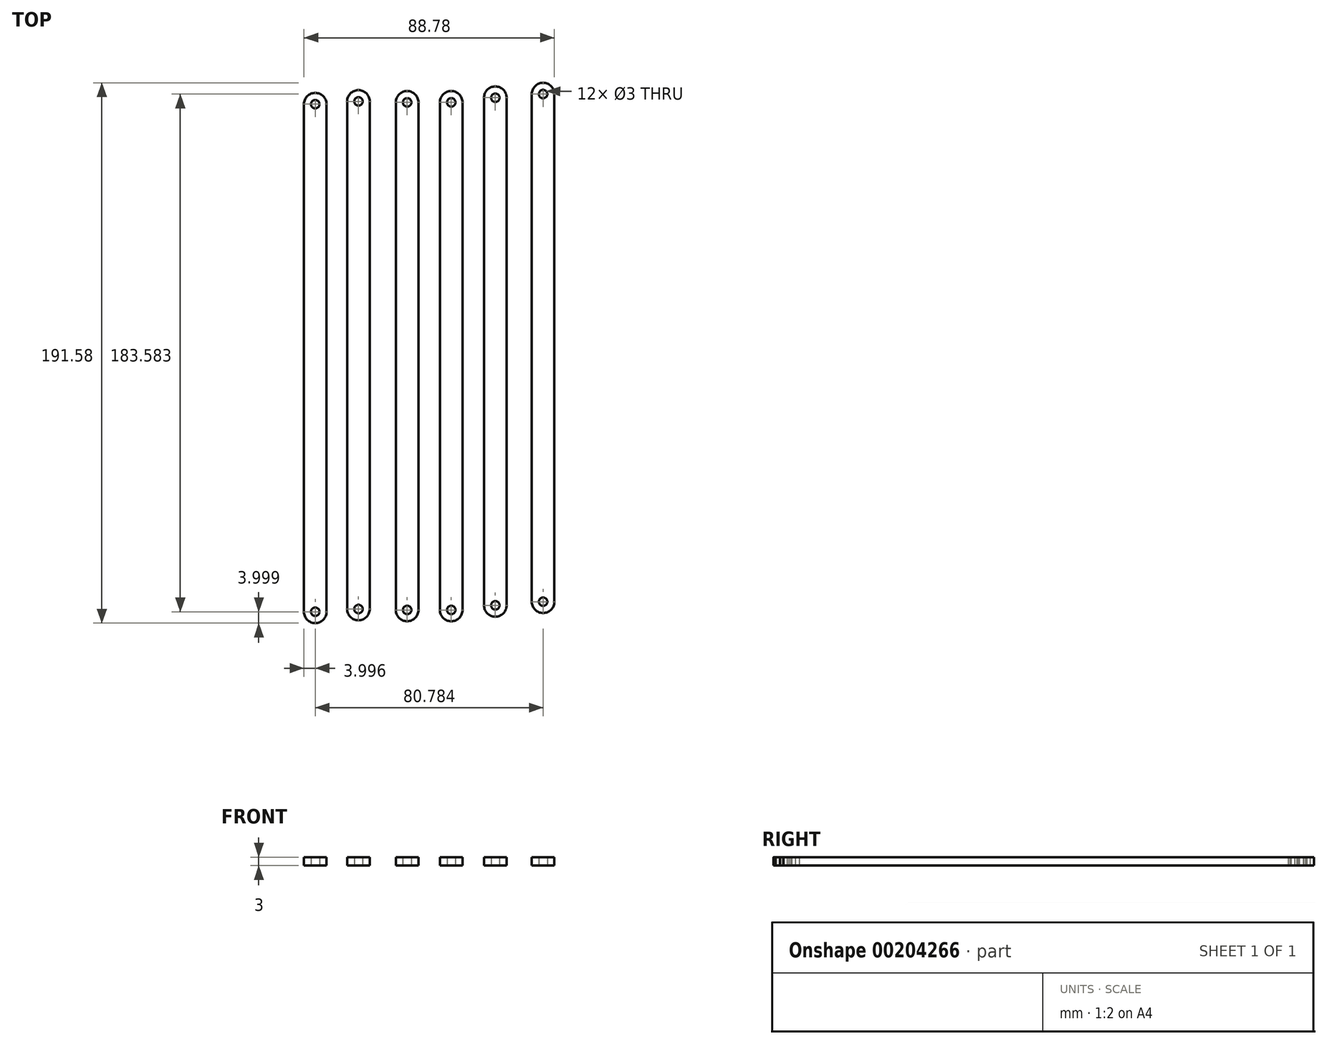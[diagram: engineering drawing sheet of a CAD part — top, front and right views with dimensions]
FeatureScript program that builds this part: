
annotation { "Feature Type Name" : "Feature", "Feature Type Description" : "" }
export const myFeature = defineFeature(function(context is Context, id is Id, definition is map)
    precondition{}
    {
        {
            var Q0;
            Q0=qCreatedBy(makeId("Top.planeOp"),FACE);
            var sketch = newSketch(context, id + "F0", { "sketchPlane" : qUnion([Q0])});
            skLineSegment(sketch, "E0", {"start": v(0, 90) * mm, "end": v(0, -90) * mm, "construction": true});
            skArc(sketch, "E1", {"start": v(4, 90) * mm, "mid": v(0, 94) * mm, "end": v(-4, 90) * mm});
            skArc(sketch, "E2", {"start": v(-4, -90) * mm, "mid": v(0, -94) * mm, "end": v(4, -90) * mm});
            skLineSegment(sketch, "E3", {"start": v(-4, 90) * mm, "end": v(-4, -90) * mm});
            skLineSegment(sketch, "E4.MirrorCS", {"start": v(4, 90) * mm, "end": v(4, -90) * mm});
            skCircle(sketch, "E5", {"center": v(0, 90) * mm, "radius": 1.5 * mm});
            skCircle(sketch, "E6", {"center": v(0, -90) * mm, "radius": 1.5 * mm});
            skLineSegment(sketch, "E7", {"start": v(-17.26, 90.33) * mm, "end": v(-17.26, -89.67) * mm, "construction": true});
            skArc(sketch, "E8", {"start": v(-13.26, 90.33) * mm, "mid": v(-17.26, 94.33) * mm, "end": v(-21.26, 90.33) * mm});
            skArc(sketch, "E9", {"start": v(-21.26, -89.67) * mm, "mid": v(-17.26, -93.67) * mm, "end": v(-13.26, -89.67) * mm});
            skLineSegment(sketch, "E10", {"start": v(-21.26, 90.33) * mm, "end": v(-21.26, -89.67) * mm});
            skLineSegment(sketch, "E11.MirrorCS", {"start": v(-13.26, 90.33) * mm, "end": v(-13.26, -89.67) * mm});
            skCircle(sketch, "E12", {"center": v(-17.26, 90.33) * mm, "radius": 1.5 * mm});
            skCircle(sketch, "E13", {"center": v(-17.26, -89.67) * mm, "radius": 1.5 * mm});
            skLineSegment(sketch, "E14", {"start": v(15.64, 90) * mm, "end": v(15.64, -90) * mm, "construction": true});
            skArc(sketch, "E15", {"start": v(19.64, 90) * mm, "mid": v(15.64, 94) * mm, "end": v(11.64, 90) * mm});
            skArc(sketch, "E16", {"start": v(11.64, -90) * mm, "mid": v(15.64, -94) * mm, "end": v(19.64, -90) * mm});
            skLineSegment(sketch, "E17", {"start": v(11.64, 90) * mm, "end": v(11.64, -90) * mm});
            skLineSegment(sketch, "E18.MirrorCS", {"start": v(19.64, 90) * mm, "end": v(19.64, -90) * mm});
            skCircle(sketch, "E19", {"center": v(15.64, 90) * mm, "radius": 1.5 * mm});
            skCircle(sketch, "E20", {"center": v(15.64, -90) * mm, "radius": 1.5 * mm});
            skLineSegment(sketch, "E21", {"start": v(31.27, 91.63) * mm, "end": v(31.27, -88.37) * mm, "construction": true});
            skArc(sketch, "E22", {"start": v(35.27, 91.63) * mm, "mid": v(31.27, 95.63) * mm, "end": v(27.27, 91.63) * mm});
            skArc(sketch, "E23", {"start": v(27.27, -88.37) * mm, "mid": v(31.27, -92.37) * mm, "end": v(35.27, -88.37) * mm});
            skLineSegment(sketch, "E24", {"start": v(27.27, 91.63) * mm, "end": v(27.27, -88.37) * mm});
            skLineSegment(sketch, "E25.MirrorCS", {"start": v(35.27, 91.63) * mm, "end": v(35.27, -88.37) * mm});
            skCircle(sketch, "E26", {"center": v(31.27, 91.63) * mm, "radius": 1.5 * mm});
            skCircle(sketch, "E27", {"center": v(31.27, -88.37) * mm, "radius": 1.5 * mm});
            skLineSegment(sketch, "E28", {"start": v(48.2, 92.93) * mm, "end": v(48.2, -87.07) * mm, "construction": true});
            skArc(sketch, "E29", {"start": v(52.2, 92.93) * mm, "mid": v(48.2, 96.93) * mm, "end": v(44.2, 92.93) * mm});
            skArc(sketch, "E30", {"start": v(44.2, -87.07) * mm, "mid": v(48.2, -91.07) * mm, "end": v(52.2, -87.07) * mm});
            skLineSegment(sketch, "E31", {"start": v(44.2, 92.93) * mm, "end": v(44.2, -87.07) * mm});
            skLineSegment(sketch, "E32.MirrorCS", {"start": v(52.2, 92.93) * mm, "end": v(52.2, -87.07) * mm});
            skCircle(sketch, "E33", {"center": v(48.2, 92.93) * mm, "radius": 1.5 * mm});
            skCircle(sketch, "E34", {"center": v(48.2, -87.07) * mm, "radius": 1.5 * mm});
            skLineSegment(sketch, "E35", {"start": v(-32.57, 89.35) * mm, "end": v(-32.57, -90.65) * mm, "construction": true});
            skArc(sketch, "E36", {"start": v(-28.57, 89.35) * mm, "mid": v(-32.57, 93.35) * mm, "end": v(-36.57, 89.35) * mm});
            skArc(sketch, "E37", {"start": v(-36.57, -90.65) * mm, "mid": v(-32.57, -94.65) * mm, "end": v(-28.57, -90.65) * mm});
            skLineSegment(sketch, "E38", {"start": v(-36.57, 89.35) * mm, "end": v(-36.57, -90.65) * mm});
            skLineSegment(sketch, "E39.MirrorCS", {"start": v(-28.57, 89.35) * mm, "end": v(-28.57, -90.65) * mm});
            skCircle(sketch, "E40", {"center": v(-32.57, 89.35) * mm, "radius": 1.5 * mm});
            skCircle(sketch, "E41", {"center": v(-32.57, -90.65) * mm, "radius": 1.5 * mm});
            skSolve(sketch);
        }
        {
            var Q0;
            Q0=makeQuery(id+"F0.imprint","IMPRINT",FACE,{"disambiguationData":[TD([[makeQuery(id+"F0.imprint","IMPRINT",EDGE,{"derivedFrom":sQuery(id+"F0.wireOp",EDGE,"E36")}),1.0]])]});
            var Q1;
            Q1=makeQuery(id+"F0.imprint","IMPRINT",FACE,{"disambiguationData":[TD([[makeQuery(id+"F0.imprint","IMPRINT",EDGE,{"derivedFrom":sQuery(id+"F0.wireOp",EDGE,"E8")}),1.0]])]});
            var Q2;
            Q2=makeQuery(id+"F0.imprint","IMPRINT",FACE,{"disambiguationData":[TD([[makeQuery(id+"F0.imprint","IMPRINT",EDGE,{"derivedFrom":sQuery(id+"F0.wireOp",EDGE,"E1")}),1.0]])]});
            var Q3;
            Q3=makeQuery(id+"F0.imprint","IMPRINT",FACE,{"disambiguationData":[TD([[makeQuery(id+"F0.imprint","IMPRINT",EDGE,{"derivedFrom":sQuery(id+"F0.wireOp",EDGE,"E15")}),1.0]])]});
            var Q4;
            Q4=makeQuery(id+"F0.imprint","IMPRINT",FACE,{"disambiguationData":[TD([[makeQuery(id+"F0.imprint","IMPRINT",EDGE,{"derivedFrom":sQuery(id+"F0.wireOp",EDGE,"E22")}),1.0]])]});
            var Q5;
            Q5=makeQuery(id+"F0.imprint","IMPRINT",FACE,{"disambiguationData":[TD([[makeQuery(id+"F0.imprint","IMPRINT",EDGE,{"derivedFrom":sQuery(id+"F0.wireOp",EDGE,"E29")}),1.0]])]});
            extrude(context, id + "F1", {"entities" : qUnion([Q0, Q1, Q2, Q3, Q4, Q5]), "depth" : 3 * mm});
        }
    });
